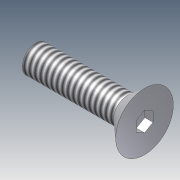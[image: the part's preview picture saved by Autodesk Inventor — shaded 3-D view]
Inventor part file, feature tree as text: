
AUTODESK INVENTOR PART (.ipt)
format: ipt  version: 2012 (Build 160160000, 160)  size: 99,840 bytes
history: native  units: in
note: dims shown in document units (in); Inventor stores cm internally (conversion verified against a paired STEP export)
features: sketch x2, revolve x1, thread x1, extrude x1
ambient origin geometry x8: Origin, YZ Plane, XZ Plane, XY Plane, X Axis, Y Axis, Z Axis, Center Point
bodies: Solid1 (feature_tree)
feature tree (5):
  revolve  "Revolution1"  [1 undecoded]
  thread  "Thread1"  [1 undecoded]
  sketch  "Sketch2"  dims[d4=90.0deg d5=1.0in d6=0.0in d16=0.1562in d17=0.075in d18=0.0in d19=1.0in]
  extrude  "Extrusion1"  Depth=1.0in TaperAngle=0.0deg
  sketch  "Sketch1"  dims[d0=0.125in d2=0.161in d3=0.2655in]
note: 2 required parameter values undecoded (feature->parameter linkage not recoverable at this tier; creation-order binding heuristic only, values carry confidence <= 0.55)